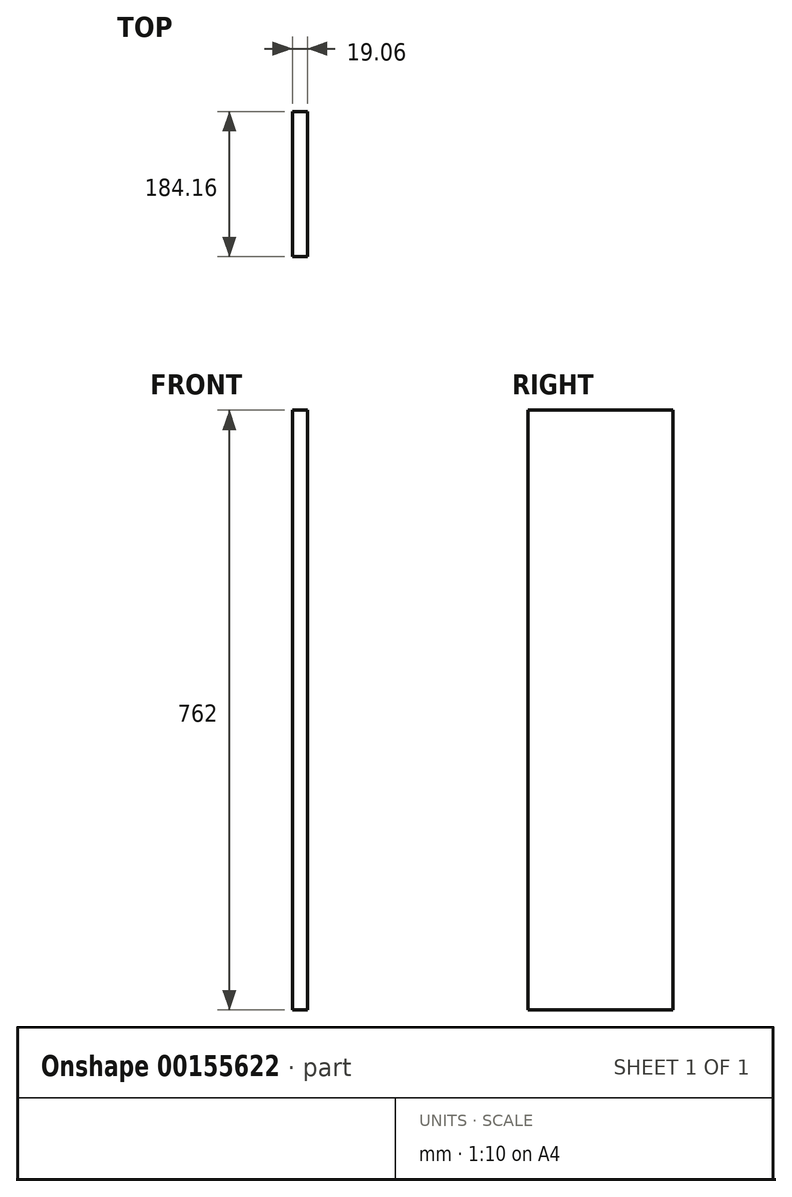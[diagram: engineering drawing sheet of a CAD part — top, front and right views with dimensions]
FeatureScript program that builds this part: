
annotation { "Feature Type Name" : "Feature", "Feature Type Description" : "" }
export const myFeature = defineFeature(function(context is Context, id is Id, definition is map)
    precondition{}
    {
        {
            var Q0;
            Q0=qCreatedBy(makeId("Top.planeOp"),FACE);
            var sketch = newSketch(context, id + "F0", { "sketchPlane" : qUnion([Q0])});
            skLineSegment(sketch, "E0.bottom", {"start": v(-9.53, 92.08) * mm, "end": v(9.52, 92.08) * mm});
            skLineSegment(sketch, "E0.top", {"start": v(-9.53, -92.08) * mm, "end": v(9.52, -92.08) * mm});
            skLineSegment(sketch, "E0.left", {"start": v(-9.53, 92.07) * mm, "end": v(-9.53, -92.08) * mm});
            skLineSegment(sketch, "E0.right", {"start": v(9.52, 92.07) * mm, "end": v(9.52, -92.08) * mm});
            skPoint(sketch, "E0.middle", {"position": v(0, 0) * mm});
            skSolve(sketch);
        }
        {
            var Q0;
            Q0=makeQuery(id+"F0.imprint","IMPRINT",FACE,{"disambiguationData":[TD([[makeQuery(id+"F0.imprint","IMPRINT",EDGE,{"derivedFrom":sQuery(id+"F0.wireOp",EDGE,"E0.bottom")}),-1.0]])]});
            extrude(context, id + "F1", {"entities" : qUnion([Q0]), "depth" : 762 * mm});
        }
    });
